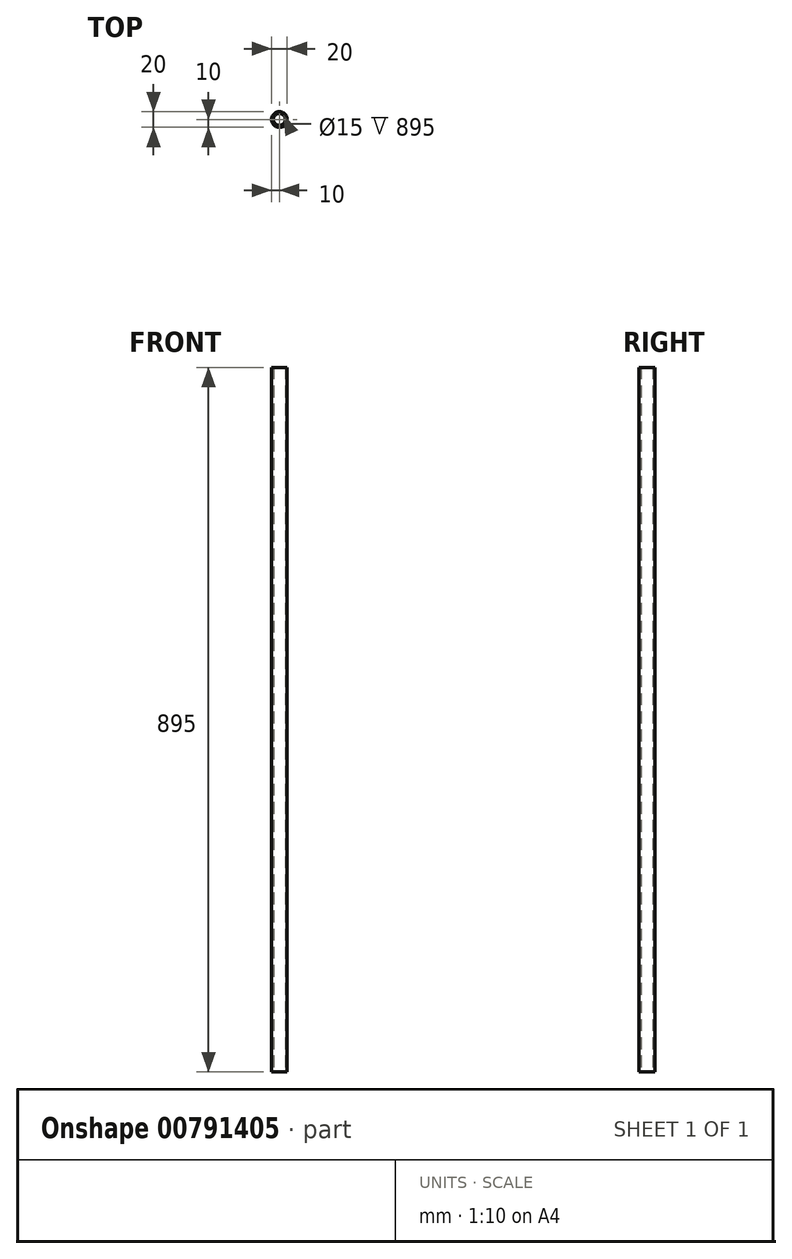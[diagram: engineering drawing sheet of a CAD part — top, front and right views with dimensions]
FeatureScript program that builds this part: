
annotation { "Feature Type Name" : "Feature", "Feature Type Description" : "" }
export const myFeature = defineFeature(function(context is Context, id is Id, definition is map)
    precondition{}
    {
        {
            var Q0;
            Q0=qCreatedBy(makeId("Top.planeOp"),FACE);
            var sketch = newSketch(context, id + "F0", { "sketchPlane" : qUnion([Q0])});
            skCircle(sketch, "E0", {"center": v(0, 0) * mm, "radius": 10 * mm});
            skCircle(sketch, "E1", {"center": v(0, 0) * mm, "radius": 7.5 * mm});
            skSolve(sketch);
        }
        {
            var Q0;
            Q0 = qSketchRegion(id + "F0", true);
            extrude(context, id + "F1", {"entities" : qUnion([Q0]), "depth" : 895 * mm, "offsetDistance" : 25 * mm});
        }
    });
